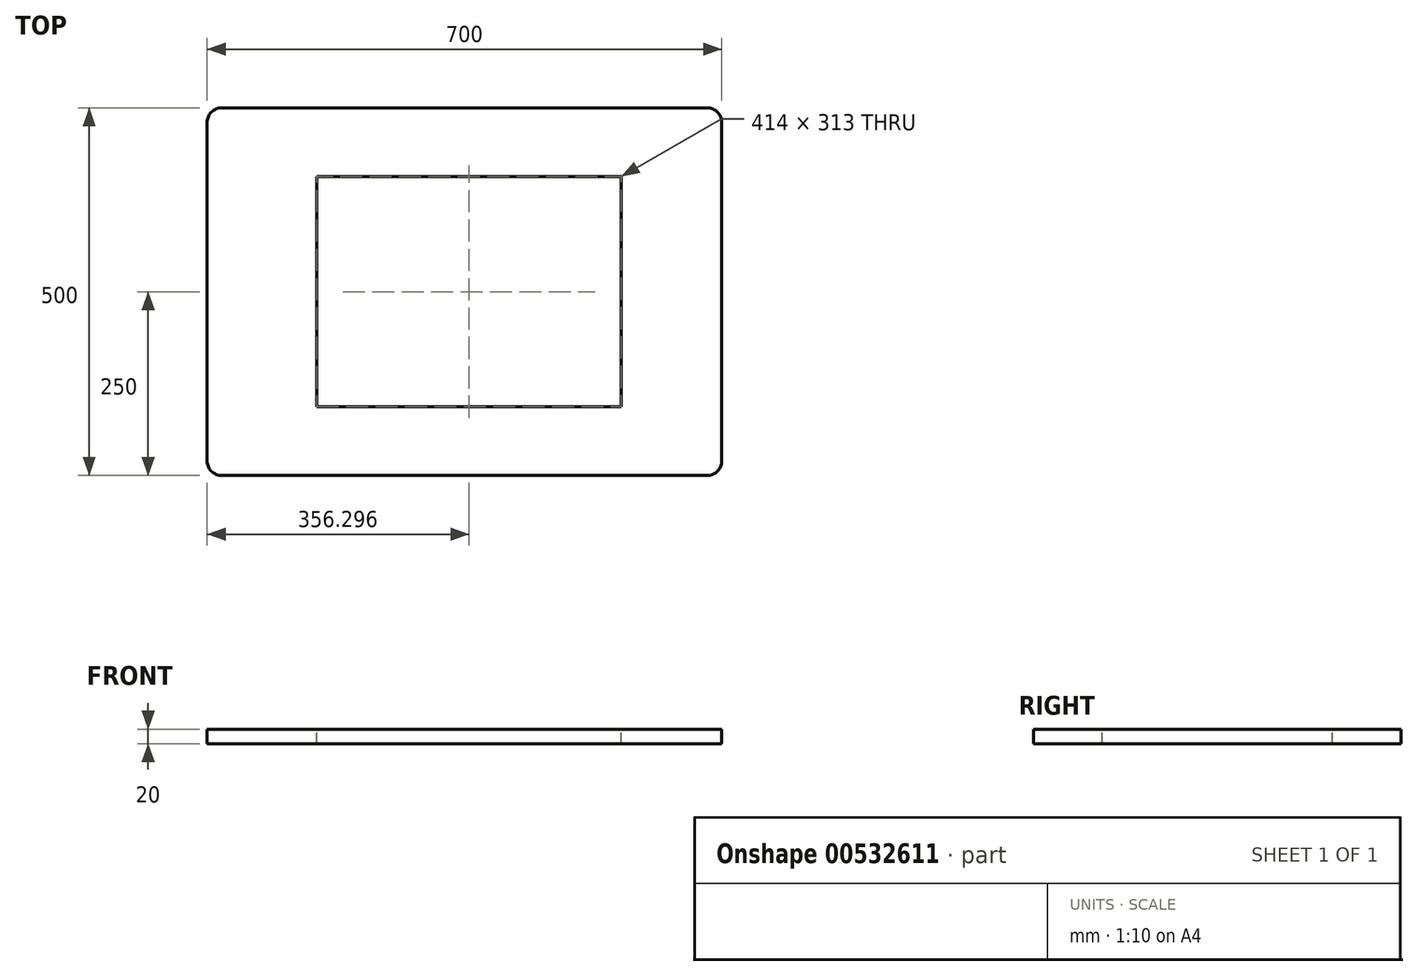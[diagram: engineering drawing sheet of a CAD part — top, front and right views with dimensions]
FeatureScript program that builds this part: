
annotation { "Feature Type Name" : "Feature", "Feature Type Description" : "" }
export const myFeature = defineFeature(function(context is Context, id is Id, definition is map)
    precondition{}
    {
        {
            var Q0;
            Q0=qCreatedBy(makeId("Top.planeOp"),FACE);
            var sketch = newSketch(context, id + "F0", { "sketchPlane" : qUnion([Q0])});
            skLineSegment(sketch, "E0.bottom", {"start": v(-350, -250) * mm, "end": v(350, -250) * mm});
            skLineSegment(sketch, "E0.top", {"start": v(-350, 250) * mm, "end": v(350, 250) * mm});
            skLineSegment(sketch, "E0.left", {"start": v(-350, -250) * mm, "end": v(-350, 250) * mm});
            skLineSegment(sketch, "E0.right", {"start": v(350, -250) * mm, "end": v(350, 250) * mm});
            skPoint(sketch, "E0.middle", {"position": v(0, 0) * mm});
            skSolve(sketch);
        }
        {
            var Q0;
            Q0=qSketchRegion(id+"F0",true);
            extrude(context, id + "F1", {"entities" : qUnion([Q0]), "depth" : 20 * mm});
        }
        {
            var Q0;
            Q0=makeQuery(id+"F1.opExtrude","CAP_FACE",FACE,{"disambiguationData":[OSD([sQuery(id+"F0.wireOp",EDGE,"E0.bottom"),sQuery(id+"F0.wireOp",EDGE,"E0.top"),sQuery(id+"F0.wireOp",EDGE,"E0.left"),sQuery(id+"F0.wireOp",EDGE,"E0.right")])],"isStart":false});
            var sketch = newSketch(context, id + "F2", { "sketchPlane" : qUnion([Q0])});
            skLineSegment(sketch, "E1.bottom", {"start": v(-200.7, 156.5) * mm, "end": v(213.3, 156.5) * mm});
            skLineSegment(sketch, "E1.top", {"start": v(-200.7, -156.5) * mm, "end": v(213.3, -156.5) * mm});
            skLineSegment(sketch, "E1.left", {"start": v(-200.7, 156.5) * mm, "end": v(-200.7, -156.5) * mm});
            skLineSegment(sketch, "E1.right", {"start": v(213.3, 156.5) * mm, "end": v(213.3, -156.5) * mm});
            skPoint(sketch, "E1.middle", {"position": v(6.3, 0) * mm});
            skSolve(sketch);
        }
        {
            var Q0;
            Q0=qSketchRegion(id+"F2",true);
            extrude(context, id + "F3", {"entities" : qUnion([Q0]), "operationType" : NewBodyOperationType.REMOVE, "endBound" : BoundingType.THROUGH_ALL, "oppositeDirection" : true, "depth" : 25 * mm});
        }
        {
            var Q0;
            Q0=makeQuery(id+"F1.opExtrude","SWEPT_EDGE",EDGE,{"disambiguationData":[OSD([sQuery(id+"F0.wireOp",EDGE,"E0.bottom"),sQuery(id+"F0.wireOp",EDGE,"E0.left")])]});
            var Q1;
            Q1=makeQuery(id+"F1.opExtrude","SWEPT_EDGE",EDGE,{"disambiguationData":[OSD([sQuery(id+"F0.wireOp",EDGE,"E0.bottom"),sQuery(id+"F0.wireOp",EDGE,"E0.right")])]});
            var Q2;
            Q2=makeQuery(id+"F1.opExtrude","SWEPT_EDGE",EDGE,{"disambiguationData":[OSD([sQuery(id+"F0.wireOp",EDGE,"E0.top"),sQuery(id+"F0.wireOp",EDGE,"E0.left")])]});
            var Q3;
            Q3=makeQuery(id+"F1.opExtrude","SWEPT_EDGE",EDGE,{"disambiguationData":[OSD([sQuery(id+"F0.wireOp",EDGE,"E0.top"),sQuery(id+"F0.wireOp",EDGE,"E0.right")])]});
            fillet(context, id + "F4", {"entities" : qUnion([Q0, Q1, Q2, Q3]), "radius" : 20 * mm, "tangentPropagation" : true, "allowEdgeOverflow" : false});
        }
    });
